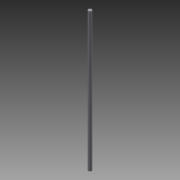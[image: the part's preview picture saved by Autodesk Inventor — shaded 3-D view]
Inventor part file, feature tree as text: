
AUTODESK INVENTOR PART (.ipt)
format: ipt  version: 2015 (Build 190159000, 159)  size: 63,488 bytes
history: native  units: in
note: dims shown in document units (in); Inventor stores cm internally (conversion verified against a paired STEP export)
features: extrude x1, sketch x1
ambient origin geometry x8: Origin, YZ Plane, XZ Plane, XY Plane, X Axis, Y Axis, Z Axis, Center Point
bodies: Solid1 (feature_tree)
feature tree (2):
  extrude  "Extrusion1"  Depth=5.0in TaperAngle=0.0deg
  sketch  "Sketch1"  dims[d0=0.125in d1=5.0in d2=0.0in]
